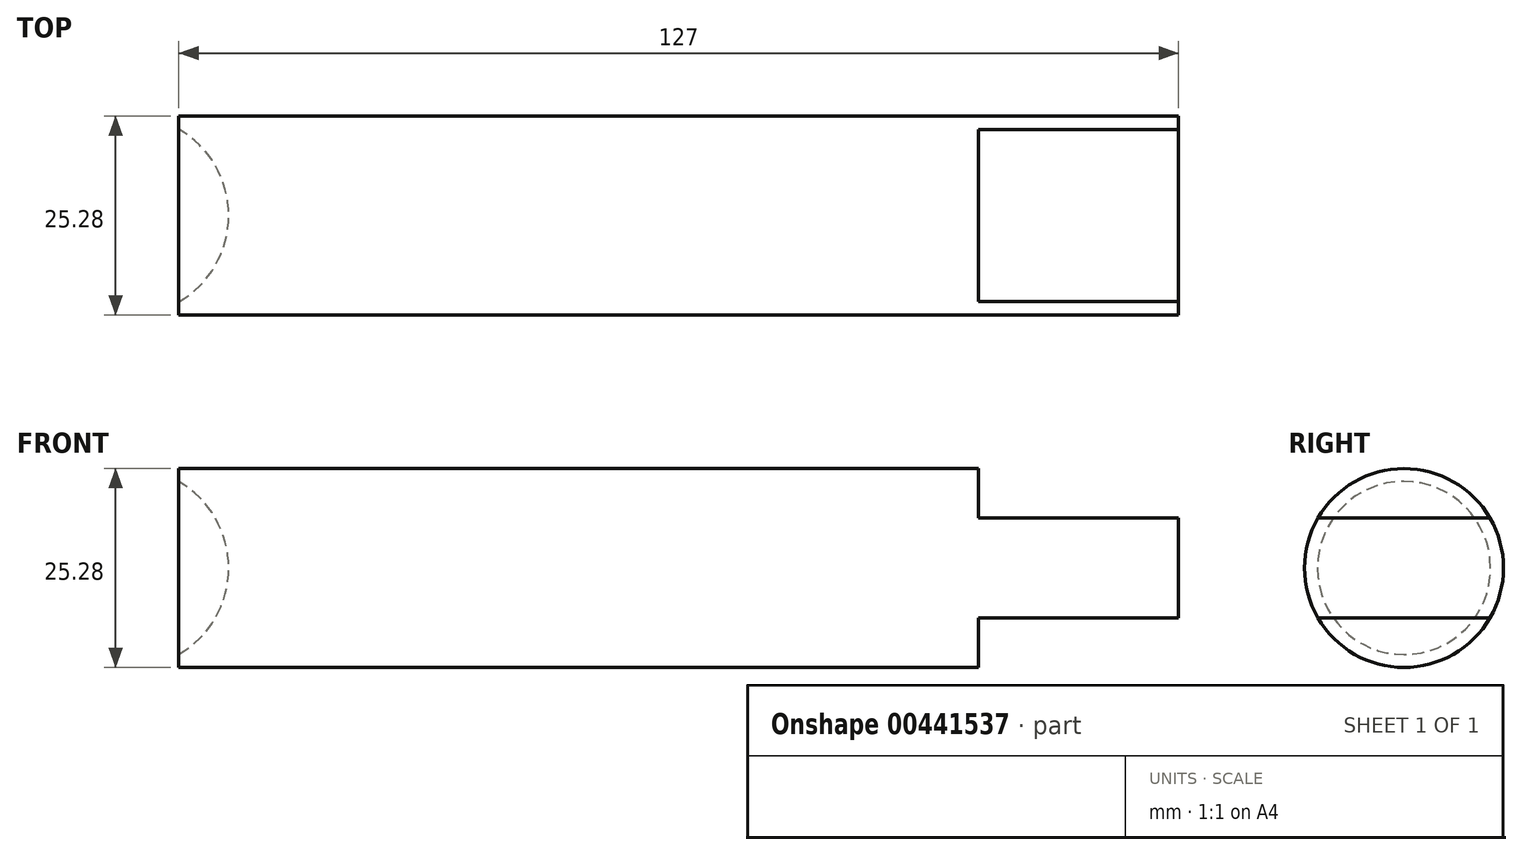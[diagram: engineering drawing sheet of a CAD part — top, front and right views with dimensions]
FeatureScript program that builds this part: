
annotation { "Feature Type Name" : "Feature", "Feature Type Description" : "" }
export const myFeature = defineFeature(function(context is Context, id is Id, definition is map)
    precondition{}
    {
        {
            var Q0;
            Q0=qCreatedBy(makeId("Right.planeOp"),FACE);
            var sketch = newSketch(context, id + "F0", { "sketchPlane" : qUnion([Q0])});
            skCircle(sketch, "E0", {"center": v(0, 0) * mm, "radius": 12.64 * mm});
            skSolve(sketch);
        }
        {
            var Q0;
            Q0=makeQuery(id+"F0.imprint","IMPRINT",FACE,{"disambiguationData":[TD([[makeQuery(id+"F0.imprint","IMPRINT",EDGE,{"derivedFrom":sQuery(id+"F0.wireOp",EDGE,"E0")}),1.0]])]});
            extrude(context, id + "F1", {"entities" : qUnion([Q0]), "endBound" : BoundingType.SYMMETRIC, "depth" : 127 * mm});
        }
        {
            var Q0;
            Q0=qCreatedBy(makeId("Front.planeOp"),FACE);
            var sketch = newSketch(context, id + "F2", { "sketchPlane" : qUnion([Q0])});
            skLineSegment(sketch, "E1", {"start": v(-63.5, 12.64) * mm, "end": v(63.5, 12.64) * mm});
            skLineSegment(sketch, "E2", {"start": v(38.1, 12.64) * mm, "end": v(38.1, 6.35) * mm});
            skLineSegment(sketch, "E3.0", {"start": v(63.5, 12.64) * mm, "end": v(63.5, -12.64) * mm});
            skLineSegment(sketch, "E4", {"start": v(38.1, 6.35) * mm, "end": v(63.5, 6.35) * mm});
            skSolve(sketch);
        }
        {
            var Q0;
            Q0 = qSketchRegion(id + "F2", true);
            extrude(context, id + "F3", {"entities" : qUnion([Q0]), "operationType" : NewBodyOperationType.REMOVE, "endBound" : BoundingType.SYMMETRIC, "oppositeDirection" : true, "depth" : 25.4 * mm});
        }
        {
            var Q0;
            Q0=qCreatedBy(makeId("Front.planeOp"),FACE);
            var sketch = newSketch(context, id + "F4", { "sketchPlane" : qUnion([Q0])});
            skLineSegment(sketch, "E5", {"start": v(-63.5, 12.64) * mm, "end": v(38.1, 12.64) * mm});
            skLineSegment(sketch, "E6.MirrorCS", {"start": v(63.5, -6.35) * mm, "end": v(38.1, -6.35) * mm});
            skLineSegment(sketch, "E7.MirrorCS", {"start": v(38.1, -12.64) * mm, "end": v(38.1, -6.35) * mm});
            skLineSegment(sketch, "E8.MirrorCS", {"start": v(-63.5, -12.64) * mm, "end": v(38.1, -12.64) * mm});
            skLineSegment(sketch, "E9", {"start": v(63.5, -6.35) * mm, "end": v(63.5, -12.64) * mm});
            skLineSegment(sketch, "E10", {"start": v(63.5, -12.64) * mm, "end": v(38.1, -12.64) * mm});
            skSolve(sketch);
        }
        {
            var Q0;
            Q0 = qSketchRegion(id + "F4", true);
            extrude(context, id + "F5", {"entities" : qUnion([Q0]), "operationType" : NewBodyOperationType.REMOVE, "endBound" : BoundingType.SYMMETRIC, "oppositeDirection" : true, "depth" : 25.4 * mm});
        }
        {
            var Q0;
            Q0=qCreatedBy(makeId("Front.planeOp"),FACE);
            var sketch = newSketch(context, id + "F6", { "sketchPlane" : qUnion([Q0])});
            skArc(sketch, "E11", {"start": v(-69.85, 12.7) * mm, "mid": v(-82.55, 0) * mm, "end": v(-69.85, -12.7) * mm});
            skLineSegment(sketch, "E12", {"start": v(-69.85, 12.7) * mm, "end": v(-69.85, -12.7) * mm});
            skSolve(sketch);
        }
        {
            var Q0;
            Q0=makeQuery(id+"F6.imprint","IMPRINT",FACE,{"disambiguationData":[TD([[makeQuery(id+"F6.imprint","IMPRINT",EDGE,{"derivedFrom":sQuery(id+"F6.wireOp",EDGE,"E11")}),1.0]])]});
            var Q1;
            Q1=sQuery(id+"F6.wireOp",EDGE,"E12");
            revolve(context, id + "F7", {"operationType" : NewBodyOperationType.REMOVE, "entities" : qUnion([Q0]), "axis" : qUnion([Q1]), "revolveType" : RevolveType.FULL, "oppositeDirection" : true});
        }
    });
